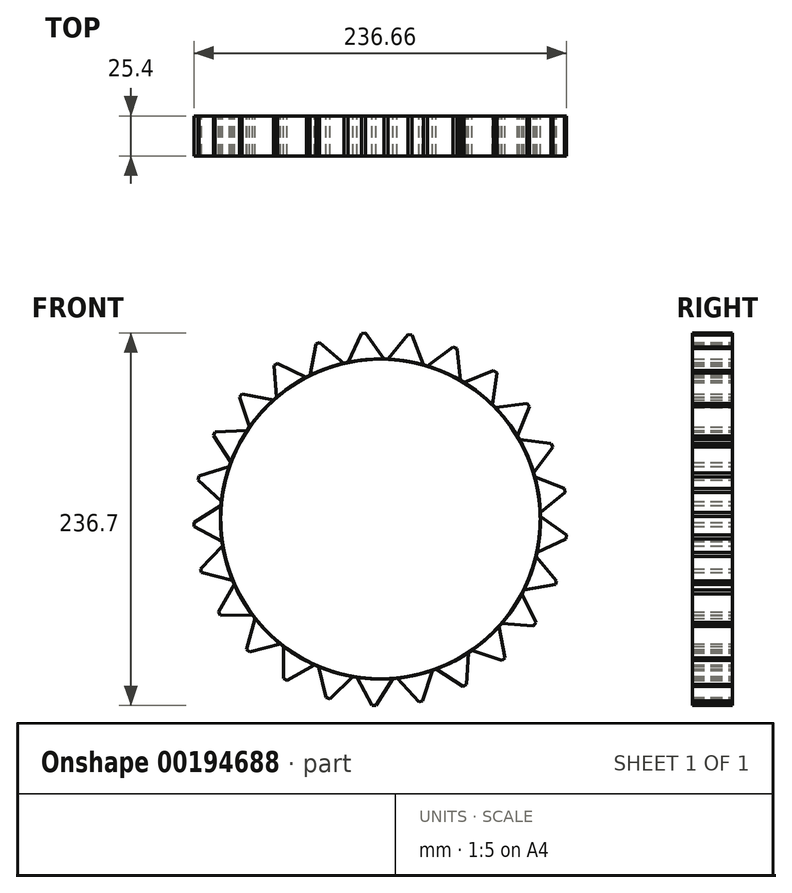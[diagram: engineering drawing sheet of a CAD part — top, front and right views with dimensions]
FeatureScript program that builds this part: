
annotation { "Feature Type Name" : "Feature", "Feature Type Description" : "" }
export const myFeature = defineFeature(function(context is Context, id is Id, definition is map)
    precondition{}
    {
        {
            var Q0;
            Q0=qCreatedBy(makeId("Front.planeOp"),FACE);
            var sketch = newSketch(context, id + "F0", { "sketchPlane" : qUnion([Q0])});
            skArc(sketch, "E0", {"start": v(101.59, 1.64) * mm, "mid": v(-101.13, 9.8) * mm, "end": v(99.38, -21.12) * mm});
            skLineSegment(sketch, "E1", {"start": v(101.59, 1.64) * mm, "end": v(118.12, -10.17) * mm});
            skLineSegment(sketch, "E2", {"start": v(118.12, -10.17) * mm, "end": v(117.88, -12.7) * mm});
            skLineSegment(sketch, "E3", {"start": v(117.88, -12.7) * mm, "end": v(99.38, -21.12) * mm});
            skSolve(sketch);
        }
        {
            var Q0;
            Q0=makeQuery(id+"F0.imprint","IMPRINT",FACE,{"disambiguationData":[TD([[makeQuery(id+"F0.imprint","IMPRINT",EDGE,{"derivedFrom":sQuery(id+"F0.wireOp",EDGE,"E0")}),1.0]])]});
            extrude(context, id + "F1", {"entities" : qUnion([Q0]), "depth" : 25.4 * mm});
        }
        {
            var Q0;
            Q0=makeQuery(id+"F1.opExtrude","SWEPT_BODY",BODY,{"disambiguationData":[OSD([sQuery(id+"F0.wireOp",EDGE,"E0"),sQuery(id+"F0.wireOp",EDGE,"E1"),sQuery(id+"F0.wireOp",EDGE,"E2"),sQuery(id+"F0.wireOp",EDGE,"E3")])]});
            var Q1;
            Q1=makeQuery(id+"F1.opExtrude","SWEPT_FACE",FACE,{"disambiguationData":[OSD([sQuery(id+"F0.wireOp",EDGE,"E0")])]});
            circularPattern(context, id + "F2", {"entities" : qUnion([Q0]), "axis" : qUnion([Q1]), "angle" : 360 * degree, "instanceCount" : 25, "equalSpace" : true});
        }
    });
